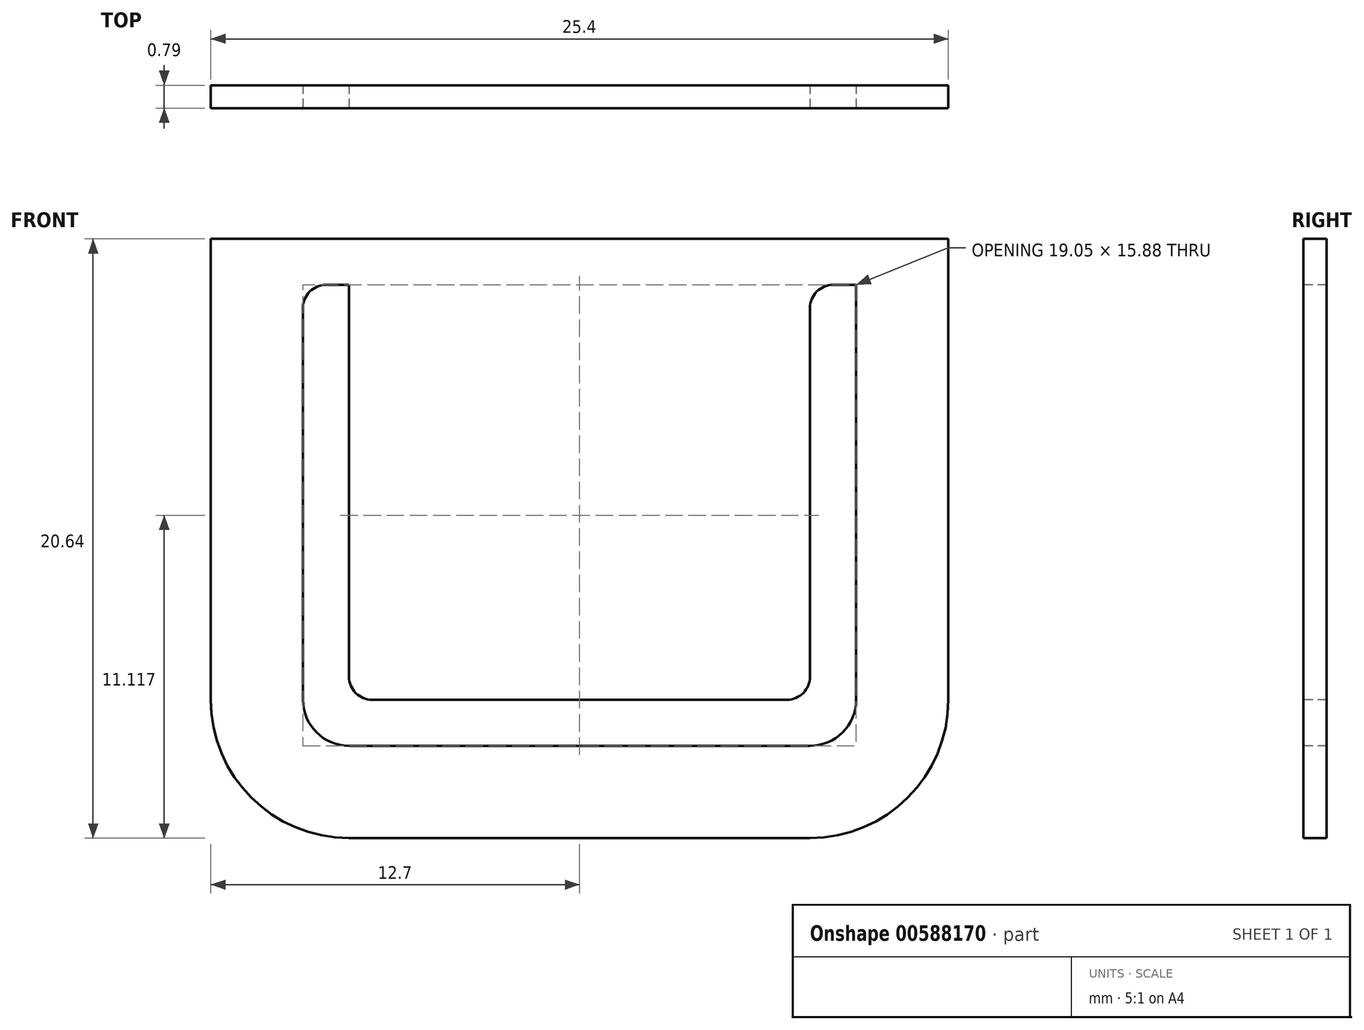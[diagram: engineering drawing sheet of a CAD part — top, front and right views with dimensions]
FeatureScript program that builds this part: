
annotation { "Feature Type Name" : "Feature", "Feature Type Description" : "" }
export const myFeature = defineFeature(function(context is Context, id is Id, definition is map)
    precondition{}
    {
        {
            var Q0;
            Q0=qCreatedBy(makeId("Front.planeOp"),FACE);
            var sketch = newSketch(context, id + "F0", { "sketchPlane" : qUnion([Q0])});
            skLineSegment(sketch, "E0.bottom", {"start": v(12.7, 9.53) * mm, "end": v(-12.7, 9.53) * mm});
            skLineSegment(sketch, "E0.top", {"start": v(12.7, -9.53) * mm, "end": v(-12.7, -9.53) * mm});
            skLineSegment(sketch, "E0.left", {"start": v(12.7, 9.53) * mm, "end": v(12.7, -9.53) * mm});
            skLineSegment(sketch, "E0.right", {"start": v(-12.7, 9.53) * mm, "end": v(-12.7, -9.53) * mm});
            skPoint(sketch, "E0.middle", {"position": v(0, 0) * mm});
            skSolve(sketch);
        }
        {
            var Q0;
            Q0=makeQuery(id+"F0.imprint","IMPRINT",FACE,{"disambiguationData":[TD([[makeQuery(id+"F0.imprint","IMPRINT",EDGE,{"derivedFrom":sQuery(id+"F0.wireOp",EDGE,"E0.bottom")}),1.0]])]});
            extrude(context, id + "F1", {"entities" : qUnion([Q0]), "depth" : 0.8 * mm, "offsetDistance" : 25.4 * mm});
        }
        {
            var Q0;
            Q0=makeQuery(id+"F1.opExtrude","SWEPT_EDGE",EDGE,{"disambiguationData":[OSD([sQuery(id+"F0.wireOp",EDGE,"E0.top"),sQuery(id+"F0.wireOp",EDGE,"E0.left")])]});
            var Q1;
            Q1=makeQuery(id+"F1.opExtrude","SWEPT_EDGE",EDGE,{"disambiguationData":[OSD([sQuery(id+"F0.wireOp",EDGE,"E0.top"),sQuery(id+"F0.wireOp",EDGE,"E0.right")])]});
            fillet(context, id + "F2", {"entities" : qUnion([Q0, Q1]), "radius" : 4.76 * mm, "tangentPropagation" : true, "allowEdgeOverflow" : false});
        }
        {
            var Q0;
            Q0=makeQuery(id+"F1.opExtrude","CAP_FACE",FACE,{"disambiguationData":[OSD([sQuery(id+"F0.wireOp",EDGE,"E0.bottom"),sQuery(id+"F0.wireOp",EDGE,"E0.top"),sQuery(id+"F0.wireOp",EDGE,"E0.left"),sQuery(id+"F0.wireOp",EDGE,"E0.right")])],"isStart":false});
            var sketch = newSketch(context, id + "F3", { "sketchPlane" : qUnion([Q0])});
            skLineSegment(sketch, "E1.bottom", {"start": v(9.52, 9.53) * mm, "end": v(-9.53, 9.53) * mm});
            skLineSegment(sketch, "E1.top", {"start": v(9.53, -6.35) * mm, "end": v(-9.53, -6.35) * mm});
            skLineSegment(sketch, "E1.left", {"start": v(9.52, 9.53) * mm, "end": v(9.53, -6.35) * mm});
            skLineSegment(sketch, "E1.right", {"start": v(-9.53, 9.53) * mm, "end": v(-9.52, -6.35) * mm});
            skPoint(sketch, "E1.middle", {"position": v(0, 0) * mm});
            skSolve(sketch);
        }
        {
            var Q0;
            Q0=makeQuery(id+"F3.imprint","IMPRINT",FACE,{"disambiguationData":[TD([[makeQuery(id+"F3.imprint","IMPRINT",EDGE,{"derivedFrom":sQuery(id+"F3.wireOp",EDGE,"E1.bottom")}),1.0]])]});
            extrude(context, id + "F4", {"entities" : qUnion([Q0]), "operationType" : NewBodyOperationType.REMOVE, "oppositeDirection" : true, "depth" : 4.93 * mm, "offsetDistance" : 25.4 * mm});
        }
        {
            var Q0;
            Q0=makeQuery(id+"F1.opExtrude","CAP_FACE",FACE,{"disambiguationData":[OSD([sQuery(id+"F0.wireOp",EDGE,"E0.bottom"),sQuery(id+"F0.wireOp",EDGE,"E0.top"),sQuery(id+"F0.wireOp",EDGE,"E0.left"),sQuery(id+"F0.wireOp",EDGE,"E0.right")])],"isStart":false});
            var sketch = newSketch(context, id + "F5", { "sketchPlane" : qUnion([Q0])});
            skLineSegment(sketch, "E2.bottom", {"start": v(-15.88, 9.53) * mm, "end": v(15.87, 9.53) * mm});
            skLineSegment(sketch, "E2.top", {"start": v(-15.88, 15.88) * mm, "end": v(15.87, 15.88) * mm});
            skLineSegment(sketch, "E2.left", {"start": v(-15.88, 9.53) * mm, "end": v(-15.88, 15.88) * mm});
            skLineSegment(sketch, "E2.right", {"start": v(15.87, 9.53) * mm, "end": v(15.87, 15.88) * mm});
            skSolve(sketch);
        }
        {
            var Q0;
            Q0=makeQuery(id+"F5.imprint","IMPRINT",FACE,{"disambiguationData":[TD([[makeQuery(id+"F5.imprint","IMPRINT",EDGE,{"derivedFrom":sQuery(id+"F5.wireOp",EDGE,"E2.top")}),-1.0]])]});
            extrude(context, id + "F6", {"entities" : qUnion([Q0]), "operationType" : NewBodyOperationType.ADD, "oppositeDirection" : true, "depth" : 0.8 * mm, "offsetDistance" : 25.4 * mm});
        }
        {
            var Q0;
            Q0=makeQuery(id+"F6.opExtrude","SWEPT_EDGE",EDGE,{"disambiguationData":[OSD([sQuery(id+"F5.wireOp",EDGE,"E2.top"),sQuery(id+"F5.wireOp",EDGE,"E2.left")])]});
            var Q1;
            Q1=makeQuery(id+"F6.opExtrude","SWEPT_EDGE",EDGE,{"disambiguationData":[OSD([sQuery(id+"F5.wireOp",EDGE,"E2.top"),sQuery(id+"F5.wireOp",EDGE,"E2.right")])]});
            var Q2;
            Q2=makeQuery(id+"F6.opExtrude","SWEPT_EDGE",EDGE,{"disambiguationData":[OSD([sQuery(id+"F5.wireOp",EDGE,"E2.bottom"),sQuery(id+"F5.wireOp",EDGE,"E2.right")])]});
            var Q3;
            Q3=makeQuery(id+"F1.opExtrude","SWEPT_EDGE",EDGE,{"disambiguationData":[OSD([sQuery(id+"F0.wireOp",EDGE,"E0.bottom"),sQuery(id+"F0.wireOp",EDGE,"E0.left")])]});
            var Q4;
            Q4=makeQuery(id+"F6.opExtrude","SWEPT_EDGE",EDGE,{"disambiguationData":[OSD([sQuery(id+"F5.wireOp",EDGE,"E2.bottom"),sQuery(id+"F5.wireOp",EDGE,"E2.left")])]});
            var Q5;
            Q5=makeQuery(id+"F1.opExtrude","SWEPT_EDGE",EDGE,{"disambiguationData":[OSD([sQuery(id+"F0.wireOp",EDGE,"E0.bottom"),sQuery(id+"F0.wireOp",EDGE,"E0.right")])]});
            fillet(context, id + "F7", {"entities" : qUnion([Q0, Q1, Q2, Q3, Q4, Q5]), "radius" : 1.59 * mm, "tangentPropagation" : true, "allowEdgeOverflow" : false});
        }
        {
            var Q0;
            Q0=makeQuery(id+"F4.boolean.opBoolean","COPY",EDGE,{"derivedFrom":makeQuery(id+"F4.opExtrude","SWEPT_EDGE",EDGE,{"disambiguationData":[OSD([sQuery(id+"F3.wireOp",EDGE,"E1.top"),sQuery(id+"F3.wireOp",EDGE,"E1.right")])]})});
            var Q1;
            Q1=makeQuery(id+"F4.boolean.opBoolean","COPY",EDGE,{"derivedFrom":makeQuery(id+"F4.opExtrude","SWEPT_EDGE",EDGE,{"disambiguationData":[OSD([sQuery(id+"F3.wireOp",EDGE,"E1.top"),sQuery(id+"F3.wireOp",EDGE,"E1.left")])]})});
            fillet(context, id + "F8", {"entities" : qUnion([Q0, Q1]), "radius" : 1.59 * mm, "tangentPropagation" : true, "allowEdgeOverflow" : false});
        }
        {
            var Q0;
            Q0=makeQuery(id+"F6.boolean.opBoolean","MERGE",FACE,{"derivedFrom":[makeQuery(id+"F1.opExtrude","CAP_FACE",FACE,{"disambiguationData":[OSD([sQuery(id+"F0.wireOp",EDGE,"E0.bottom"),sQuery(id+"F0.wireOp",EDGE,"E0.top"),sQuery(id+"F0.wireOp",EDGE,"E0.left"),sQuery(id+"F0.wireOp",EDGE,"E0.right")])],"isStart":false}),makeQuery(id+"F6.opExtrude","CAP_FACE",FACE,{"disambiguationData":[OSD([sQuery(id+"F5.wireOp",EDGE,"E2.bottom"),sQuery(id+"F5.wireOp",EDGE,"E2.top"),sQuery(id+"F5.wireOp",EDGE,"E2.left"),sQuery(id+"F5.wireOp",EDGE,"E2.right")])],"isStart":true})]});
            var sketch = newSketch(context, id + "F9", { "sketchPlane" : qUnion([Q0])});
            skLineSegment(sketch, "E3.bottom", {"start": v(-7.94, 9.53) * mm, "end": v(7.94, 9.53) * mm});
            skLineSegment(sketch, "E3.top", {"start": v(-7.94, -4.76) * mm, "end": v(7.94, -4.76) * mm});
            skLineSegment(sketch, "E3.left", {"start": v(-7.94, 9.53) * mm, "end": v(-7.94, -4.76) * mm});
            skLineSegment(sketch, "E3.right", {"start": v(7.94, 9.53) * mm, "end": v(7.94, -4.76) * mm});
            skSolve(sketch);
        }
        {
            var Q0;
            Q0=makeQuery(id+"F9.imprint","IMPRINT",FACE,{"disambiguationData":[TD([[makeQuery(id+"F9.imprint","IMPRINT",EDGE,{"derivedFrom":sQuery(id+"F9.wireOp",EDGE,"E3.bottom")}),1.0]])]});
            extrude(context, id + "F10", {"entities" : qUnion([Q0]), "operationType" : NewBodyOperationType.ADD, "oppositeDirection" : true, "depth" : 0.8 * mm, "offsetDistance" : 25.4 * mm});
        }
        {
            var Q0;
            Q0=makeQuery(id+"F10.opExtrude","SWEPT_EDGE",EDGE,{"disambiguationData":[OSD([sQuery(id+"F5.wireOp",EDGE,"E2.bottom"),sQuery(id+"F9.wireOp",EDGE,"E3.bottom"),sQuery(id+"F9.wireOp",EDGE,"E3.left")])]});
            var Q1;
            Q1=makeQuery(id+"F4.boolean.opBoolean","COPY",EDGE,{"derivedFrom":makeQuery(id+"F4.opExtrude","SWEPT_EDGE",EDGE,{"disambiguationData":[OSD([sQuery(id+"F0.wireOp",EDGE,"E0.bottom"),sQuery(id+"F3.wireOp",EDGE,"E1.bottom"),sQuery(id+"F3.wireOp",EDGE,"E1.right")])]})});
            var Q2;
            Q2=makeQuery(id+"F10.opExtrude","SWEPT_EDGE",EDGE,{"disambiguationData":[OSD([sQuery(id+"F5.wireOp",EDGE,"E2.bottom"),sQuery(id+"F9.wireOp",EDGE,"E3.bottom"),sQuery(id+"F9.wireOp",EDGE,"E3.right")])]});
            var Q3;
            Q3=makeQuery(id+"F4.boolean.opBoolean","COPY",EDGE,{"derivedFrom":makeQuery(id+"F4.opExtrude","SWEPT_EDGE",EDGE,{"disambiguationData":[OSD([sQuery(id+"F0.wireOp",EDGE,"E0.bottom"),sQuery(id+"F3.wireOp",EDGE,"E1.bottom"),sQuery(id+"F3.wireOp",EDGE,"E1.left")])]})});
            fillet(context, id + "F11", {"entities" : qUnion([Q0, Q1, Q2, Q3]), "radius" : 0.8 * mm, "tangentPropagation" : true, "allowEdgeOverflow" : false});
        }
        {
            var Q0;
            Q0=makeQuery(id+"F10.opExtrude","SWEPT_EDGE",EDGE,{"disambiguationData":[OSD([sQuery(id+"F9.wireOp",EDGE,"E3.top"),sQuery(id+"F9.wireOp",EDGE,"E3.left")])]});
            var Q1;
            Q1=makeQuery(id+"F10.opExtrude","SWEPT_EDGE",EDGE,{"disambiguationData":[OSD([sQuery(id+"F9.wireOp",EDGE,"E3.top"),sQuery(id+"F9.wireOp",EDGE,"E3.right")])]});
            fillet(context, id + "F12", {"entities" : qUnion([Q0, Q1]), "radius" : 0.8 * mm, "tangentPropagation" : true, "allowEdgeOverflow" : false});
        }
        {
            var Q0;
            Q0=makeQuery(id+"F10.boolean.opBoolean","MERGE",FACE,{"derivedFrom":[makeQuery(id+"F6.boolean.opBoolean","MERGE",FACE,{"derivedFrom":[makeQuery(id+"F1.opExtrude","CAP_FACE",FACE,{"disambiguationData":[OSD([sQuery(id+"F0.wireOp",EDGE,"E0.bottom"),sQuery(id+"F0.wireOp",EDGE,"E0.top"),sQuery(id+"F0.wireOp",EDGE,"E0.left"),sQuery(id+"F0.wireOp",EDGE,"E0.right")])],"isStart":false}),makeQuery(id+"F6.opExtrude","CAP_FACE",FACE,{"disambiguationData":[OSD([sQuery(id+"F5.wireOp",EDGE,"E2.bottom"),sQuery(id+"F5.wireOp",EDGE,"E2.top"),sQuery(id+"F5.wireOp",EDGE,"E2.left"),sQuery(id+"F5.wireOp",EDGE,"E2.right")])],"isStart":true})]}),makeQuery(id+"F10.opExtrude","CAP_FACE",FACE,{"disambiguationData":[OSD([sQuery(id+"F9.wireOp",EDGE,"E3.bottom"),sQuery(id+"F9.wireOp",EDGE,"E3.top"),sQuery(id+"F9.wireOp",EDGE,"E3.left"),sQuery(id+"F9.wireOp",EDGE,"E3.right")])],"isStart":true})]});
            var sketch = newSketch(context, id + "F13", { "sketchPlane" : qUnion([Q0])});
            skPoint(sketch, "E4.0", {"position": v(-12.7, 7.94) * mm});
            skLineSegment(sketch, "E5.bottom", {"start": v(-12.7, 7.94) * mm, "end": v(-17.26, 7.94) * mm});
            skLineSegment(sketch, "E5.top", {"start": v(-12.7, 16.66) * mm, "end": v(-17.26, 16.66) * mm});
            skLineSegment(sketch, "E5.left", {"start": v(-12.7, 7.94) * mm, "end": v(-12.7, 16.66) * mm});
            skLineSegment(sketch, "E5.right", {"start": v(-17.26, 7.94) * mm, "end": v(-17.26, 16.66) * mm});
            skLineSegment(sketch, "E6.bottom", {"start": v(12.7, 7.94) * mm, "end": v(16.72, 7.94) * mm});
            skLineSegment(sketch, "E6.top", {"start": v(12.7, 16.94) * mm, "end": v(16.72, 16.94) * mm});
            skLineSegment(sketch, "E6.left", {"start": v(12.7, 7.94) * mm, "end": v(12.7, 16.94) * mm});
            skLineSegment(sketch, "E6.right", {"start": v(16.72, 7.94) * mm, "end": v(16.72, 16.94) * mm});
            skSolve(sketch);
        }
        {
            var Q0;
            Q0=makeQuery(id+"F13.imprint","IMPRINT",FACE,{"disambiguationData":[TD([[makeQuery(id+"F13.imprint","IMPRINT",EDGE,{"derivedFrom":sQuery(id+"F13.wireOp",EDGE,"E5.bottom")}),-1.0]])]});
            var Q1;
            {var subQ0=sQuery(id+"F5.wireOp",EDGE,"E2.left");Q1=makeQuery(id+"F13.imprint","IMPRINT",FACE,{"disambiguationData":[TD([[makeQuery(id+"F13.imprint","IMPRINT",EDGE,{"derivedFrom":makeQuery(id+"F6.opExtrude","CAP_EDGE",EDGE,{"disambiguationData":[OSD([subQ0])],"isStart":true})}),-1.0]])]});}
            var Q2;
            {var subQ0=sQuery(id+"F5.wireOp",EDGE,"E2.right");Q2=makeQuery(id+"F13.imprint","IMPRINT",FACE,{"disambiguationData":[TD([[makeQuery(id+"F13.imprint","IMPRINT",EDGE,{"derivedFrom":makeQuery(id+"F6.opExtrude","CAP_EDGE",EDGE,{"disambiguationData":[OSD([subQ0])],"isStart":true})}),1.0]])]});}
            var Q3;
            Q3=makeQuery(id+"F13.imprint","IMPRINT",FACE,{"disambiguationData":[TD([[makeQuery(id+"F13.imprint","IMPRINT",EDGE,{"derivedFrom":sQuery(id+"F13.wireOp",EDGE,"E6.bottom")}),1.0]])]});
            extrude(context, id + "F14", {"entities" : qUnion([Q0, Q1, Q2, Q3]), "operationType" : NewBodyOperationType.REMOVE, "oppositeDirection" : true, "depth" : 25.4 * mm, "offsetDistance" : 25.4 * mm});
        }
        {
            var Q0;
            Q0=makeQuery(id+"F10.boolean.opBoolean","MERGE",FACE,{"derivedFrom":[makeQuery(id+"F6.boolean.opBoolean","MERGE",FACE,{"derivedFrom":[makeQuery(id+"F1.opExtrude","CAP_FACE",FACE,{"disambiguationData":[OSD([sQuery(id+"F0.wireOp",EDGE,"E0.bottom"),sQuery(id+"F0.wireOp",EDGE,"E0.top"),sQuery(id+"F0.wireOp",EDGE,"E0.left"),sQuery(id+"F0.wireOp",EDGE,"E0.right")])],"isStart":false}),makeQuery(id+"F6.opExtrude","CAP_FACE",FACE,{"disambiguationData":[OSD([sQuery(id+"F5.wireOp",EDGE,"E2.bottom"),sQuery(id+"F5.wireOp",EDGE,"E2.top"),sQuery(id+"F5.wireOp",EDGE,"E2.left"),sQuery(id+"F5.wireOp",EDGE,"E2.right")])],"isStart":true})]}),makeQuery(id+"F10.opExtrude","CAP_FACE",FACE,{"disambiguationData":[OSD([sQuery(id+"F9.wireOp",EDGE,"E3.bottom"),sQuery(id+"F9.wireOp",EDGE,"E3.top"),sQuery(id+"F9.wireOp",EDGE,"E3.left"),sQuery(id+"F9.wireOp",EDGE,"E3.right")])],"isStart":true})]});
            var sketch = newSketch(context, id + "F15", { "sketchPlane" : qUnion([Q0])});
            skLineSegment(sketch, "E7.bottom", {"start": v(-12.7, 15.88) * mm, "end": v(12.7, 15.88) * mm});
            skLineSegment(sketch, "E7.top", {"start": v(-12.7, 11.11) * mm, "end": v(12.7, 11.11) * mm});
            skLineSegment(sketch, "E7.left", {"start": v(-12.7, 15.88) * mm, "end": v(-12.7, 11.11) * mm});
            skLineSegment(sketch, "E7.right", {"start": v(12.7, 15.88) * mm, "end": v(12.7, 11.11) * mm});
            skSolve(sketch);
        }
        {
            var Q0;
            Q0=makeQuery(id+"F15.imprint","IMPRINT",FACE,{"disambiguationData":[TD([[makeQuery(id+"F15.imprint","IMPRINT",EDGE,{"derivedFrom":sQuery(id+"F15.wireOp",EDGE,"E7.bottom")}),-1.0]])]});
            extrude(context, id + "F16", {"entities" : qUnion([Q0]), "operationType" : NewBodyOperationType.REMOVE, "oppositeDirection" : true, "depth" : 25.4 * mm, "offsetDistance" : 25.4 * mm});
        }
    });
